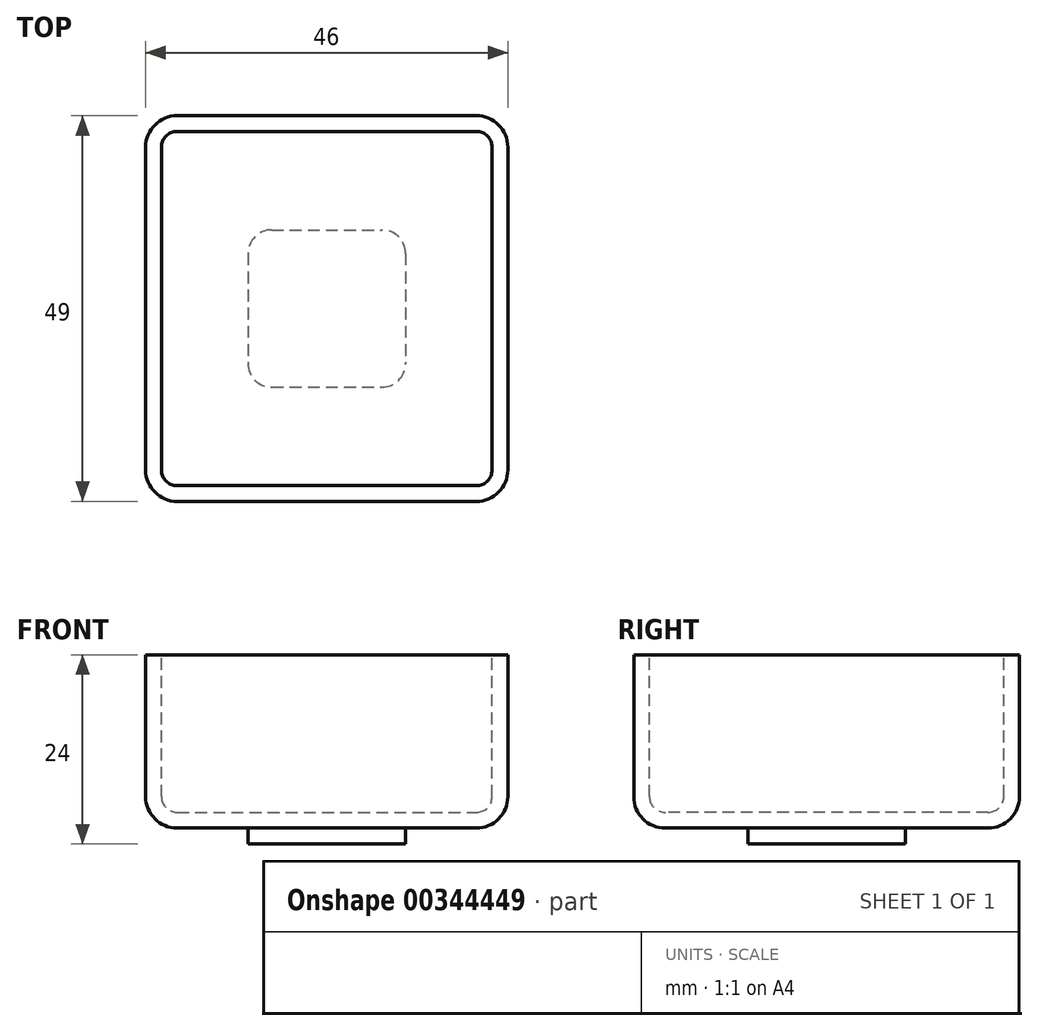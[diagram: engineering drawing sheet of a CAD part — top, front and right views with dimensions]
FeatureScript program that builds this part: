
annotation { "Feature Type Name" : "Feature", "Feature Type Description" : "" }
export const myFeature = defineFeature(function(context is Context, id is Id, definition is map)
    precondition{}
    {
        {
            var Q0;
            Q0=qCreatedBy(makeId("Top.planeOp"),FACE);
            var sketch = newSketch(context, id + "F0", { "sketchPlane" : qUnion([Q0])});
            skLineSegment(sketch, "E0.bottom", {"start": v(-7, 10) * mm, "end": v(7, 10) * mm});
            skLineSegment(sketch, "E0.top", {"start": v(-7, -10) * mm, "end": v(7, -10) * mm});
            skLineSegment(sketch, "E0.left", {"start": v(-10, 7) * mm, "end": v(-10, -7) * mm});
            skLineSegment(sketch, "E0.right", {"start": v(10, 7) * mm, "end": v(10, -7) * mm});
            skPoint(sketch, "E1", {"position": v(0, 10) * mm});
            skPoint(sketch, "E2", {"position": v(10, 0) * mm});
            skPoint(sketch, "E3.visualSharp", {"position": v(-10, 10) * mm});
            skArc(sketch, "E3.filletArc", {"start": v(-7, 10) * mm, "mid": v(-9.12, 9.12) * mm, "end": v(-10, 7) * mm});
            skPoint(sketch, "E4.visualSharp", {"position": v(10, 10) * mm});
            skArc(sketch, "E4.filletArc", {"start": v(10, 7) * mm, "mid": v(9.12, 9.12) * mm, "end": v(7, 10) * mm});
            skPoint(sketch, "E5.visualSharp", {"position": v(10, -10) * mm});
            skArc(sketch, "E5.filletArc", {"start": v(7, -10) * mm, "mid": v(9.12, -9.12) * mm, "end": v(10, -7) * mm});
            skPoint(sketch, "E6.visualSharp", {"position": v(-10, -10) * mm});
            skArc(sketch, "E6.filletArc", {"start": v(-10, -7) * mm, "mid": v(-9.12, -9.12) * mm, "end": v(-7, -10) * mm});
            skSolve(sketch);
        }
        {
            var Q0;
            Q0 = qSketchRegion(id + "F0", true);
            extrude(context, id + "F1", {"entities" : qUnion([Q0]), "depth" : 2 * mm});
        }
        {
            var Q0;
            Q0=makeQuery(id+"F1.opExtrude","CAP_FACE",FACE,{"disambiguationData":[OSD([sQuery(id+"F0.wireOp",EDGE,"E0.bottom"),sQuery(id+"F0.wireOp",EDGE,"E0.top"),sQuery(id+"F0.wireOp",EDGE,"E0.left"),sQuery(id+"F0.wireOp",EDGE,"E0.right"),sQuery(id+"F0.wireOp",EDGE,"E3.filletArc"),sQuery(id+"F0.wireOp",EDGE,"E4.filletArc"),sQuery(id+"F0.wireOp",EDGE,"E5.filletArc"),sQuery(id+"F0.wireOp",EDGE,"E6.filletArc")])],"isStart":false});
            var sketch = newSketch(context, id + "F2", { "sketchPlane" : qUnion([Q0])});
            skLineSegment(sketch, "E7.bottom", {"start": v(-23, 24.5) * mm, "end": v(23, 24.5) * mm});
            skLineSegment(sketch, "E7.top", {"start": v(-23, -24.5) * mm, "end": v(23, -24.5) * mm});
            skLineSegment(sketch, "E7.left", {"start": v(-23, 24.5) * mm, "end": v(-23, -24.5) * mm});
            skLineSegment(sketch, "E7.right", {"start": v(23, 24.5) * mm, "end": v(23, -24.5) * mm});
            skPoint(sketch, "E8", {"position": v(0, 24.5) * mm});
            skPoint(sketch, "E9", {"position": v(23, 0) * mm});
            skSolve(sketch);
        }
        {
            var Q0;
            Q0=makeQuery(id+"F2.imprint","IMPRINT",FACE,{"disambiguationData":[TD([[makeQuery(id+"F2.imprint","IMPRINT",EDGE,{"derivedFrom":sQuery(id+"F2.wireOp",EDGE,"E7.bottom")}),-1.0]])]});
            var Q1;
            Q1=makeQuery(id+"F2.imprint","IMPRINT",FACE,{"disambiguationData":[TD([[makeQuery(id+"F2.imprint","IMPRINT",EDGE,{"derivedFrom":makeQuery(id+"F1.opExtrude","CAP_EDGE",EDGE,{"disambiguationData":[OSD([sQuery(id+"F0.wireOp",EDGE,"E0.bottom")])],"isStart":false})}),-1.0]])]});
            extrude(context, id + "F3", {"entities" : qUnion([Q0, Q1]), "operationType" : NewBodyOperationType.ADD, "depth" : 22 * mm});
        }
        {
            var Q0;
            Q0=makeQuery(id+"F3.opExtrude","CAP_FACE",FACE,{"disambiguationData":[OSD([sQuery(id+"F2.wireOp",EDGE,"E7.bottom"),sQuery(id+"F2.wireOp",EDGE,"E7.top"),sQuery(id+"F2.wireOp",EDGE,"E7.left"),sQuery(id+"F2.wireOp",EDGE,"E7.right")])],"isStart":false});
            var sketch = newSketch(context, id + "F4", { "sketchPlane" : qUnion([Q0])});
            skLineSegment(sketch, "E10.bottom", {"start": v(-21, 22.5) * mm, "end": v(21, 22.5) * mm});
            skLineSegment(sketch, "E10.top", {"start": v(-21, -22.5) * mm, "end": v(21, -22.5) * mm});
            skLineSegment(sketch, "E10.left", {"start": v(-21, 22.5) * mm, "end": v(-21, -22.5) * mm});
            skLineSegment(sketch, "E10.right", {"start": v(21, 22.5) * mm, "end": v(21, -22.5) * mm});
            skPoint(sketch, "E11", {"position": v(21, 0) * mm});
            skPoint(sketch, "E12", {"position": v(0, 22.5) * mm});
            skSolve(sketch);
        }
        {
            var Q0;
            Q0=makeQuery(id+"F4.imprint","IMPRINT",FACE,{"disambiguationData":[TD([[makeQuery(id+"F4.imprint","IMPRINT",EDGE,{"derivedFrom":sQuery(id+"F4.wireOp",EDGE,"E10.bottom")}),-1.0]])]});
            extrude(context, id + "F5", {"entities" : qUnion([Q0]), "operationType" : NewBodyOperationType.REMOVE, "oppositeDirection" : true, "depth" : 20 * mm});
        }
        {
            var Q0;
            Q0=makeQuery(id+"F3.opExtrude","SWEPT_EDGE",EDGE,{"disambiguationData":[OSD([sQuery(id+"F2.wireOp",EDGE,"E7.bottom"),sQuery(id+"F2.wireOp",EDGE,"E7.left")])]});
            var Q1;
            Q1=makeQuery(id+"F3.opExtrude","SWEPT_EDGE",EDGE,{"disambiguationData":[OSD([sQuery(id+"F2.wireOp",EDGE,"E7.bottom"),sQuery(id+"F2.wireOp",EDGE,"E7.right")])]});
            var Q2;
            Q2=makeQuery(id+"F3.opExtrude","SWEPT_EDGE",EDGE,{"disambiguationData":[OSD([sQuery(id+"F2.wireOp",EDGE,"E7.top"),sQuery(id+"F2.wireOp",EDGE,"E7.right")])]});
            var Q3;
            Q3=makeQuery(id+"F3.opExtrude","SWEPT_EDGE",EDGE,{"disambiguationData":[OSD([sQuery(id+"F2.wireOp",EDGE,"E7.top"),sQuery(id+"F2.wireOp",EDGE,"E7.left")])]});
            fillet(context, id + "F6", {"entities" : qUnion([Q0, Q1, Q2, Q3]), "radius" : 4 * mm, "tangentPropagation" : true, "allowEdgeOverflow" : false});
        }
        {
            var Q0;
            Q0=makeQuery(id+"F5.boolean.opBoolean","COPY",EDGE,{"derivedFrom":makeQuery(id+"F5.opExtrude","SWEPT_EDGE",EDGE,{"disambiguationData":[OSD([sQuery(id+"F4.wireOp",EDGE,"E10.bottom"),sQuery(id+"F4.wireOp",EDGE,"E10.right")])]})});
            var Q1;
            Q1=makeQuery(id+"F5.boolean.opBoolean","COPY",EDGE,{"derivedFrom":makeQuery(id+"F5.opExtrude","SWEPT_EDGE",EDGE,{"disambiguationData":[OSD([sQuery(id+"F4.wireOp",EDGE,"E10.top"),sQuery(id+"F4.wireOp",EDGE,"E10.right")])]})});
            var Q2;
            Q2=makeQuery(id+"F5.boolean.opBoolean","COPY",EDGE,{"derivedFrom":makeQuery(id+"F5.opExtrude","SWEPT_EDGE",EDGE,{"disambiguationData":[OSD([sQuery(id+"F4.wireOp",EDGE,"E10.top"),sQuery(id+"F4.wireOp",EDGE,"E10.left")])]})});
            var Q3;
            Q3=makeQuery(id+"F5.boolean.opBoolean","COPY",EDGE,{"derivedFrom":makeQuery(id+"F5.opExtrude","SWEPT_EDGE",EDGE,{"disambiguationData":[OSD([sQuery(id+"F4.wireOp",EDGE,"E10.bottom"),sQuery(id+"F4.wireOp",EDGE,"E10.left")])]})});
            fillet(context, id + "F7", {"entities" : qUnion([Q0, Q1, Q2, Q3]), "radius" : 2 * mm, "tangentPropagation" : true, "allowEdgeOverflow" : false});
        }
        {
            var Q0;
            Q0=makeQuery(id+"F5.boolean.opBoolean","COPY",FACE,{"derivedFrom":makeQuery(id+"F5.opExtrude","CAP_FACE",FACE,{"disambiguationData":[OSD([sQuery(id+"F4.wireOp",EDGE,"E10.bottom"),sQuery(id+"F4.wireOp",EDGE,"E10.top"),sQuery(id+"F4.wireOp",EDGE,"E10.left"),sQuery(id+"F4.wireOp",EDGE,"E10.right")])],"isStart":false})});
            fillet(context, id + "F8", {"entities" : qUnion([Q0]), "radius" : 2 * mm, "tangentPropagation" : true, "allowEdgeOverflow" : false});
        }
        {
            var Q0;
            Q0=makeQuery(id+"F3.opExtrude","CAP_EDGE",EDGE,{"disambiguationData":[OSD([sQuery(id+"F2.wireOp",EDGE,"E7.bottom")])],"isStart":true});
            var Q1;
            {var subQ0=sQuery(id+"F2.wireOp",EDGE,"E7.left");var subQ1=sQuery(id+"F2.wireOp",EDGE,"E7.bottom");Q1=makeQuery(id+"F6.opFillet","BLEND_EDGE",EDGE,{"blendedFrom":[makeQuery(id+"F3.opExtrude","SWEPT_EDGE",EDGE,{"disambiguationData":[OSD([subQ1,subQ0])]}),makeQuery(id+"F3.opExtrude","CAP_FACE",FACE,{"disambiguationData":[OSD([subQ1,sQuery(id+"F2.wireOp",EDGE,"E7.top"),subQ0,sQuery(id+"F2.wireOp",EDGE,"E7.right")])],"isStart":true})],"blendedInto":[makeQuery(id+"F3.opExtrude","CAP_FACE",FACE,{"disambiguationData":[OSD([subQ1,sQuery(id+"F2.wireOp",EDGE,"E7.top"),subQ0,sQuery(id+"F2.wireOp",EDGE,"E7.right")])],"isStart":true})]});}
            var Q2;
            Q2=makeQuery(id+"F3.opExtrude","CAP_EDGE",EDGE,{"disambiguationData":[OSD([sQuery(id+"F2.wireOp",EDGE,"E7.left")])],"isStart":true});
            var Q3;
            {var subQ0=sQuery(id+"F2.wireOp",EDGE,"E7.left");var subQ1=sQuery(id+"F2.wireOp",EDGE,"E7.top");Q3=makeQuery(id+"F6.opFillet","BLEND_EDGE",EDGE,{"blendedFrom":[makeQuery(id+"F3.opExtrude","SWEPT_EDGE",EDGE,{"disambiguationData":[OSD([subQ1,subQ0])]}),makeQuery(id+"F3.opExtrude","CAP_FACE",FACE,{"disambiguationData":[OSD([sQuery(id+"F2.wireOp",EDGE,"E7.bottom"),subQ1,subQ0,sQuery(id+"F2.wireOp",EDGE,"E7.right")])],"isStart":true})],"blendedInto":[makeQuery(id+"F3.opExtrude","CAP_FACE",FACE,{"disambiguationData":[OSD([sQuery(id+"F2.wireOp",EDGE,"E7.bottom"),subQ1,subQ0,sQuery(id+"F2.wireOp",EDGE,"E7.right")])],"isStart":true})]});}
            var Q4;
            Q4=makeQuery(id+"F3.opExtrude","CAP_EDGE",EDGE,{"disambiguationData":[OSD([sQuery(id+"F2.wireOp",EDGE,"E7.top")])],"isStart":true});
            var Q5;
            {var subQ0=sQuery(id+"F2.wireOp",EDGE,"E7.right");var subQ1=sQuery(id+"F2.wireOp",EDGE,"E7.top");Q5=makeQuery(id+"F6.opFillet","BLEND_EDGE",EDGE,{"blendedFrom":[makeQuery(id+"F3.opExtrude","SWEPT_EDGE",EDGE,{"disambiguationData":[OSD([subQ1,subQ0])]}),makeQuery(id+"F3.opExtrude","CAP_FACE",FACE,{"disambiguationData":[OSD([sQuery(id+"F2.wireOp",EDGE,"E7.bottom"),subQ1,sQuery(id+"F2.wireOp",EDGE,"E7.left"),subQ0])],"isStart":true})],"blendedInto":[makeQuery(id+"F3.opExtrude","CAP_FACE",FACE,{"disambiguationData":[OSD([sQuery(id+"F2.wireOp",EDGE,"E7.bottom"),subQ1,sQuery(id+"F2.wireOp",EDGE,"E7.left"),subQ0])],"isStart":true})]});}
            var Q6;
            Q6=makeQuery(id+"F3.opExtrude","CAP_EDGE",EDGE,{"disambiguationData":[OSD([sQuery(id+"F2.wireOp",EDGE,"E7.right")])],"isStart":true});
            var Q7;
            {var subQ0=sQuery(id+"F2.wireOp",EDGE,"E7.right");var subQ1=sQuery(id+"F2.wireOp",EDGE,"E7.bottom");Q7=makeQuery(id+"F6.opFillet","BLEND_EDGE",EDGE,{"blendedFrom":[makeQuery(id+"F3.opExtrude","SWEPT_EDGE",EDGE,{"disambiguationData":[OSD([subQ1,subQ0])]}),makeQuery(id+"F3.opExtrude","CAP_FACE",FACE,{"disambiguationData":[OSD([subQ1,sQuery(id+"F2.wireOp",EDGE,"E7.top"),sQuery(id+"F2.wireOp",EDGE,"E7.left"),subQ0])],"isStart":true})],"blendedInto":[makeQuery(id+"F3.opExtrude","CAP_FACE",FACE,{"disambiguationData":[OSD([subQ1,sQuery(id+"F2.wireOp",EDGE,"E7.top"),sQuery(id+"F2.wireOp",EDGE,"E7.left"),subQ0])],"isStart":true})]});}
            fillet(context, id + "F9", {"entities" : qUnion([Q0, Q1, Q2, Q3, Q4, Q5, Q6, Q7]), "radius" : 4 * mm, "tangentPropagation" : true, "allowEdgeOverflow" : false});
        }
    });
